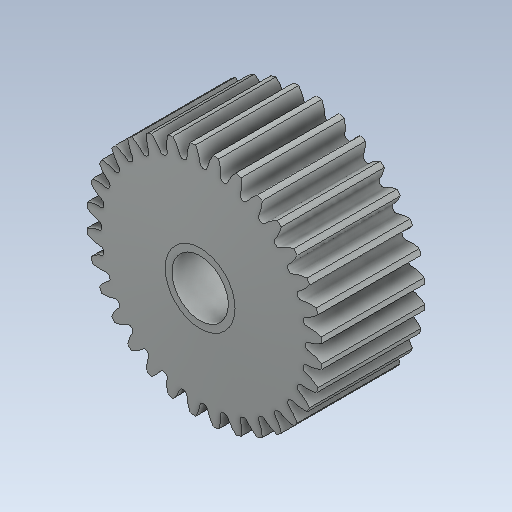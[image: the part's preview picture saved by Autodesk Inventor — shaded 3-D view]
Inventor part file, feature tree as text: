
AUTODESK INVENTOR PART (.ipt)
format: ipt  version: 2020 (Build 240168000, 168)  size: 516,608 bytes
history: native  units: in
note: dims shown in document units (in); Inventor stores cm internally (conversion verified against a paired STEP export)
features: mirror x1
ambient origin geometry x8: Origin, YZ Plane, XZ Plane, XY Plane, X Axis, Y Axis, Z Axis, Center Point
bodies: Solid1 (feature_tree)
feature tree (1):
  mirror  "Mirror1"
